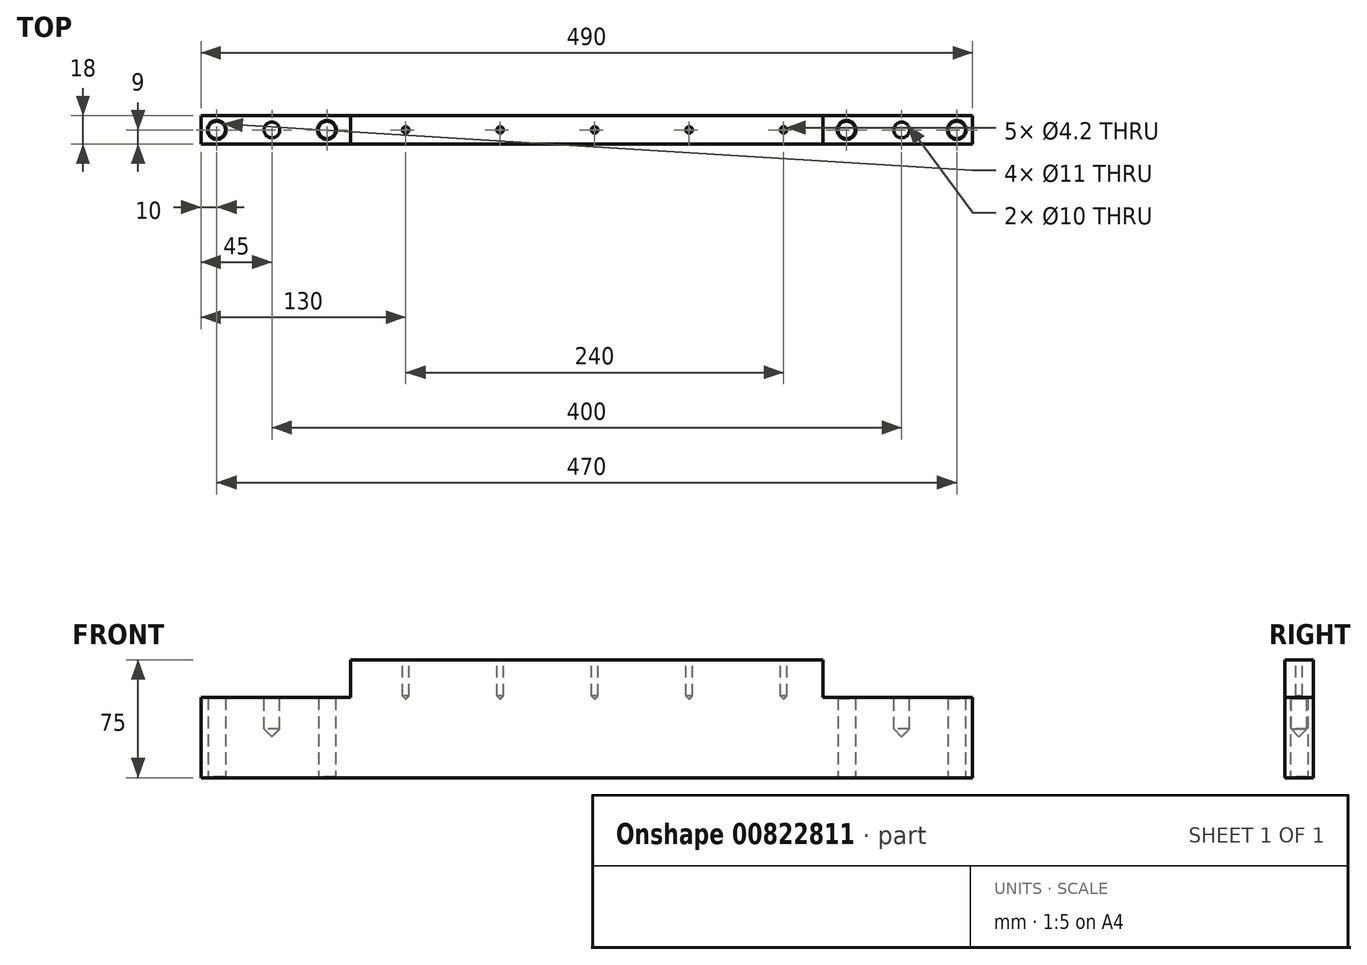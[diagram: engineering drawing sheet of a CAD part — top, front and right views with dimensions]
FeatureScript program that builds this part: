
annotation { "Feature Type Name" : "Feature", "Feature Type Description" : "" }
export const myFeature = defineFeature(function(context is Context, id is Id, definition is map)
    precondition{}
    {
        {
            var Q0;
            Q0=qCreatedBy(makeId("Front.planeOp"),FACE);
            var sketch = newSketch(context, id + "F0", { "sketchPlane" : qUnion([Q0])});
            skLineSegment(sketch, "E0.bottom", {"start": v(-245, -37.5) * mm, "end": v(245, -37.5) * mm});
            skLineSegment(sketch, "E0.top", {"start": v(-150, 37.5) * mm, "end": v(150, 37.5) * mm});
            skLineSegment(sketch, "E0.left", {"start": v(-245, -37.5) * mm, "end": v(-245, 13.5) * mm});
            skLineSegment(sketch, "E0.right", {"start": v(245, -37.5) * mm, "end": v(245, 13.5) * mm});
            skPoint(sketch, "E0.middle", {"position": v(0, 0) * mm});
            skLineSegment(sketch, "E1", {"start": v(-245, 13.5) * mm, "end": v(-150, 13.5) * mm});
            skLineSegment(sketch, "E2", {"start": v(-150, 13.5) * mm, "end": v(-150, 37.5) * mm});
            skLineSegment(sketch, "E3", {"start": v(0, 0) * mm, "end": v(0, 109.73) * mm, "construction": true});
            skPoint(sketch, "E3.endSnap0", {"position": v(0, 37.5) * mm});
            skLineSegment(sketch, "E4.MirrorCS", {"start": v(245, 13.5) * mm, "end": v(150, 13.5) * mm});
            skLineSegment(sketch, "E5.MirrorCS", {"start": v(150, 13.5) * mm, "end": v(150, 37.5) * mm});
            skPoint(sketch, "E6.orphan", {"position": v(-245, 37.5) * mm});
            skPoint(sketch, "E7.orphan", {"position": v(245, 37.5) * mm});
            skSolve(sketch);
        }
        {
            var Q0;
            Q0 = qSketchRegion(id + "F0", true);
            extrude(context, id + "F1", {"entities" : qUnion([Q0]), "endBound" : BoundingType.SYMMETRIC, "depth" : 18 * mm, "offsetDistance" : 25 * mm});
        }
        {
            var Q0;
            Q0=makeQuery(id+"F1.opExtrude","SWEPT_FACE",FACE,{"disambiguationData":[OSD([sQuery(id+"F0.wireOp",EDGE,"E0.bottom")])]});
            var sketch = newSketch(context, id + "F2", { "sketchPlane" : qUnion([Q0])});
            skLineSegment(sketch, "E8", {"start": v(0, 0) * mm, "end": v(0, 32.03) * mm, "construction": true});
            skLineSegment(sketch, "E9", {"start": v(0, 32.03) * mm, "end": v(235, 0) * mm, "construction": true});
            skLineSegment(sketch, "E10", {"start": v(235, 0) * mm, "end": v(0, 0) * mm, "construction": true});
            skCircle(sketch, "E11", {"center": v(235, 0) * mm, "radius": 5.5 * mm});
            skCircle(sketch, "E12", {"center": v(165, 0) * mm, "radius": 5.5 * mm});
            skCircle(sketch, "E13.MirrorC", {"center": v(-165, 0) * mm, "radius": 5.5 * mm});
            skCircle(sketch, "E14.MirrorC", {"center": v(-235, 0) * mm, "radius": 5.5 * mm});
            skSolve(sketch);
        }
        {
            var Q0;
            Q0 = qSketchRegion(id + "F2", true);
            extrude(context, id + "F3", {"entities" : qUnion([Q0]), "operationType" : NewBodyOperationType.REMOVE, "endBound" : BoundingType.UP_TO_NEXT, "oppositeDirection" : true, "depth" : 25 * mm, "offsetDistance" : 25 * mm});
        }
        {
            var Q0;
            Q0=makeQuery(id+"F1.opExtrude","SWEPT_FACE",FACE,{"disambiguationData":[OSD([sQuery(id+"F0.wireOp",EDGE,"E0.top")])]});
            var sketch = newSketch(context, id + "F4", { "sketchPlane" : qUnion([Q0])});
            skLineSegment(sketch, "E15", {"start": v(0, 0) * mm, "end": v(-175, 0) * mm, "construction": true});
            skLineSegment(sketch, "E16.0", {"start": v(-150, -9) * mm, "end": v(-150, 9) * mm, "construction": true});
            skCircle(sketch, "E17", {"center": v(-175, 0) * mm, "radius": 2.1 * mm, "construction": true});
            skLineSegment(sketch, "E18", {"start": v(-175, 0) * mm, "end": v(-195, 0) * mm, "construction": true});
            skCircle(sketch, "E19.1.0.0", {"center": v(-115, 0) * mm, "radius": 2.1 * mm});
            skCircle(sketch, "E19.2.0.0", {"center": v(-55, 0) * mm, "radius": 2.1 * mm});
            skCircle(sketch, "E19.3.0.0", {"center": v(5, 0) * mm, "radius": 2.1 * mm});
            skCircle(sketch, "E19.4.0.0", {"center": v(65, 0) * mm, "radius": 2.1 * mm});
            skCircle(sketch, "E19.5.0.0", {"center": v(125, 0) * mm, "radius": 2.1 * mm});
            skCircle(sketch, "E19.6.0.0", {"center": v(185, 0) * mm, "radius": 2.1 * mm, "construction": true});
            skCircle(sketch, "E19.7.0.0", {"center": v(245, 0) * mm, "radius": 2.1 * mm, "construction": true});
            skCircle(sketch, "E19.8.0.0", {"center": v(305, 0) * mm, "radius": 2.1 * mm, "construction": true});
            skLineSegment(sketch, "E19.direction1", {"start": v(-175, 0) * mm, "end": v(-115, 0) * mm, "construction": true});
            skLineSegment(sketch, "E20", {"start": v(0, 0) * mm, "end": v(0, 52.01) * mm, "construction": true});
            skLineSegment(sketch, "E21", {"start": v(0, 52.01) * mm, "end": v(-62, 56.3) * mm, "construction": true});
            skLineSegment(sketch, "E22", {"start": v(-62, 56.3) * mm, "end": v(-62, -65.3) * mm, "construction": true});
            skLineSegment(sketch, "E23.bottom", {"start": v(-24.5, 38.85) * mm, "end": v(-99.5, 38.85) * mm});
            skLineSegment(sketch, "E23.top", {"start": v(-24.5, -169.44) * mm, "end": v(-99.5, -169.44) * mm, "construction": true});
            skLineSegment(sketch, "E23.left", {"start": v(-24.5, 38.85) * mm, "end": v(-24.5, -169.44) * mm, "construction": true});
            skLineSegment(sketch, "E23.right", {"start": v(-99.5, 38.85) * mm, "end": v(-99.5, -169.44) * mm, "construction": true});
            skPoint(sketch, "E23.middle", {"position": v(-62, -65.3) * mm});
            skLineSegment(sketch, "E24.bottom", {"start": v(-112.5, 84.27) * mm, "end": v(-187.5, 84.27) * mm, "construction": true});
            skLineSegment(sketch, "E24.top", {"start": v(-112.5, -270.84) * mm, "end": v(-187.5, -270.84) * mm, "construction": true});
            skLineSegment(sketch, "E24.left", {"start": v(-112.5, 84.27) * mm, "end": v(-112.5, -270.84) * mm, "construction": true});
            skLineSegment(sketch, "E24.right", {"start": v(-187.5, 84.27) * mm, "end": v(-187.5, -270.84) * mm, "construction": true});
            skPoint(sketch, "E24.middle", {"position": v(-150, -93.28) * mm});
            skLineSegment(sketch, "E25", {"start": v(-150, -93.28) * mm, "end": v(0, -93.28) * mm, "construction": true});
            skLineSegment(sketch, "E26", {"start": v(0, -93.28) * mm, "end": v(0, 0) * mm, "construction": true});
            skSolve(sketch);
        }
        {
            var Q0;
            Q0 = qSketchRegion(id + "F4", true);
            extrude(context, id + "F5", {"entities" : qUnion([Q0]), "operationType" : NewBodyOperationType.REMOVE, "oppositeDirection" : true, "depth" : 25 * mm, "offsetDistance" : 25 * mm});
        }
        {
            var Q0;
            Q0=makeQuery(id+"F1.opExtrude","SWEPT_FACE",FACE,{"disambiguationData":[OSD([sQuery(id+"F0.wireOp",EDGE,"E1")])]});
            var sketch = newSketch(context, id + "F6", { "sketchPlane" : qUnion([Q0])});
            skLineSegment(sketch, "E27", {"start": v(0, 0) * mm, "end": v(-200, 0) * mm, "construction": true});
            skCircle(sketch, "E28", {"center": v(-200, 0) * mm, "radius": 5 * mm});
            skCircle(sketch, "E29.0", {"center": v(-165, 0) * mm, "radius": 5.5 * mm, "construction": true});
            skCircle(sketch, "E30.0", {"center": v(-235, 0) * mm, "radius": 5.5 * mm, "construction": true});
            skLineSegment(sketch, "E31", {"start": v(0, 0) * mm, "end": v(0, -60.15) * mm, "construction": true});
            skCircle(sketch, "E32.MirrorC", {"center": v(200, 0) * mm, "radius": 5 * mm});
            skSolve(sketch);
        }
        {
            var Q0;
            Q0 = qSketchRegion(id + "F6", true);
            extrude(context, id + "F7", {"entities" : qUnion([Q0]), "operationType" : NewBodyOperationType.REMOVE, "oppositeDirection" : true, "depth" : 25 * mm, "offsetDistance" : 25 * mm});
        }
        {
            var Q0;
            Q0=makeQuery(id+"F7.boolean.opBoolean","COPY",FACE,{"derivedFrom":makeQuery(id+"F7.opExtrude","CAP_FACE",FACE,{"disambiguationData":[OSD([sQuery(id+"F6.wireOp",EDGE,"E28")])],"isStart":false})});
            var Q1;
            Q1=makeQuery(id+"F7.boolean.opBoolean","COPY",FACE,{"derivedFrom":makeQuery(id+"F7.opExtrude","CAP_FACE",FACE,{"disambiguationData":[OSD([sQuery(id+"F6.wireOp",EDGE,"E32.MirrorC")])],"isStart":false})});
            chamfer(context, id + "F8", {"entities" : qUnion([Q0, Q1]), "width" : 5 * mm, "tangentPropagation" : true});
        }
        {
            var Q0;
            Q0=makeQuery(id+"F5.boolean.opBoolean","COPY",FACE,{"derivedFrom":makeQuery(id+"F5.opExtrude","CAP_FACE",FACE,{"disambiguationData":[OSD([sQuery(id+"F4.wireOp",EDGE,"E19.5.0.0")])],"isStart":false})});
            var Q1;
            Q1=makeQuery(id+"F5.boolean.opBoolean","COPY",FACE,{"derivedFrom":makeQuery(id+"F5.opExtrude","CAP_FACE",FACE,{"disambiguationData":[OSD([sQuery(id+"F4.wireOp",EDGE,"E19.4.0.0")])],"isStart":false})});
            var Q2;
            Q2=makeQuery(id+"F5.boolean.opBoolean","COPY",FACE,{"derivedFrom":makeQuery(id+"F5.opExtrude","CAP_FACE",FACE,{"disambiguationData":[OSD([sQuery(id+"F4.wireOp",EDGE,"E19.3.0.0")])],"isStart":false})});
            var Q3;
            Q3=makeQuery(id+"F5.boolean.opBoolean","COPY",FACE,{"derivedFrom":makeQuery(id+"F5.opExtrude","CAP_FACE",FACE,{"disambiguationData":[OSD([sQuery(id+"F4.wireOp",EDGE,"E19.2.0.0")])],"isStart":false})});
            var Q4;
            Q4=makeQuery(id+"F5.boolean.opBoolean","COPY",FACE,{"derivedFrom":makeQuery(id+"F5.opExtrude","CAP_FACE",FACE,{"disambiguationData":[OSD([sQuery(id+"F4.wireOp",EDGE,"E19.1.0.0")])],"isStart":false})});
            chamfer(context, id + "F9", {"entities" : qUnion([Q0, Q1, Q2, Q3, Q4]), "width" : 2.1 * mm, "tangentPropagation" : true});
        }
        {
            var Q0;
            Q0=makeQuery(id+"F3.boolean.opBoolean","COPY",FACE,{"derivedFrom":makeQuery(id+"F3.opExtrude","SWEPT_FACE",FACE,{"disambiguationData":[OSD([sQuery(id+"F2.wireOp",EDGE,"E13.MirrorC")])]})});
            var Q1;
            Q1=makeQuery(id+"F3.boolean.opBoolean","COPY",FACE,{"derivedFrom":makeQuery(id+"F3.opExtrude","SWEPT_FACE",FACE,{"disambiguationData":[OSD([sQuery(id+"F2.wireOp",EDGE,"E14.MirrorC")])]})});
            var Q2;
            Q2=makeQuery(id+"F7.boolean.opBoolean","COPY",EDGE,{"derivedFrom":makeQuery(id+"F7.opExtrude","CAP_EDGE",EDGE,{"disambiguationData":[OSD([sQuery(id+"F6.wireOp",EDGE,"E28")])],"isStart":true})});
            var Q3;
            Q3=makeQuery(id+"F5.boolean.opBoolean","COPY",EDGE,{"derivedFrom":makeQuery(id+"F5.opExtrude","CAP_EDGE",EDGE,{"disambiguationData":[OSD([sQuery(id+"F4.wireOp",EDGE,"E19.1.0.0")])],"isStart":true})});
            var Q4;
            Q4=makeQuery(id+"F5.boolean.opBoolean","COPY",EDGE,{"derivedFrom":makeQuery(id+"F5.opExtrude","CAP_EDGE",EDGE,{"disambiguationData":[OSD([sQuery(id+"F4.wireOp",EDGE,"E19.2.0.0")])],"isStart":true})});
            var Q5;
            Q5=makeQuery(id+"F5.boolean.opBoolean","COPY",EDGE,{"derivedFrom":makeQuery(id+"F5.opExtrude","CAP_EDGE",EDGE,{"disambiguationData":[OSD([sQuery(id+"F4.wireOp",EDGE,"E19.3.0.0")])],"isStart":true})});
            var Q6;
            Q6=makeQuery(id+"F5.boolean.opBoolean","COPY",EDGE,{"derivedFrom":makeQuery(id+"F5.opExtrude","CAP_EDGE",EDGE,{"disambiguationData":[OSD([sQuery(id+"F4.wireOp",EDGE,"E19.4.0.0")])],"isStart":true})});
            var Q7;
            Q7=makeQuery(id+"F5.boolean.opBoolean","COPY",EDGE,{"derivedFrom":makeQuery(id+"F5.opExtrude","CAP_EDGE",EDGE,{"disambiguationData":[OSD([sQuery(id+"F4.wireOp",EDGE,"E19.5.0.0")])],"isStart":true})});
            var Q8;
            Q8=makeQuery(id+"F3.boolean.opBoolean","COPY",FACE,{"derivedFrom":makeQuery(id+"F3.opExtrude","SWEPT_FACE",FACE,{"disambiguationData":[OSD([sQuery(id+"F2.wireOp",EDGE,"E12")])]})});
            var Q9;
            Q9=makeQuery(id+"F3.boolean.opBoolean","COPY",FACE,{"derivedFrom":makeQuery(id+"F3.opExtrude","SWEPT_FACE",FACE,{"disambiguationData":[OSD([sQuery(id+"F2.wireOp",EDGE,"E11")])]})});
            var Q10;
            Q10=makeQuery(id+"F7.boolean.opBoolean","COPY",EDGE,{"derivedFrom":makeQuery(id+"F7.opExtrude","CAP_EDGE",EDGE,{"disambiguationData":[OSD([sQuery(id+"F6.wireOp",EDGE,"E32.MirrorC")])],"isStart":true})});
            chamfer(context, id + "F10", {"entities" : qUnion([Q0, Q1, Q2, Q3, Q4, Q5, Q6, Q7, Q8, Q9, Q10]), "width" : 0.5 * mm, "tangentPropagation" : true});
        }
    });
